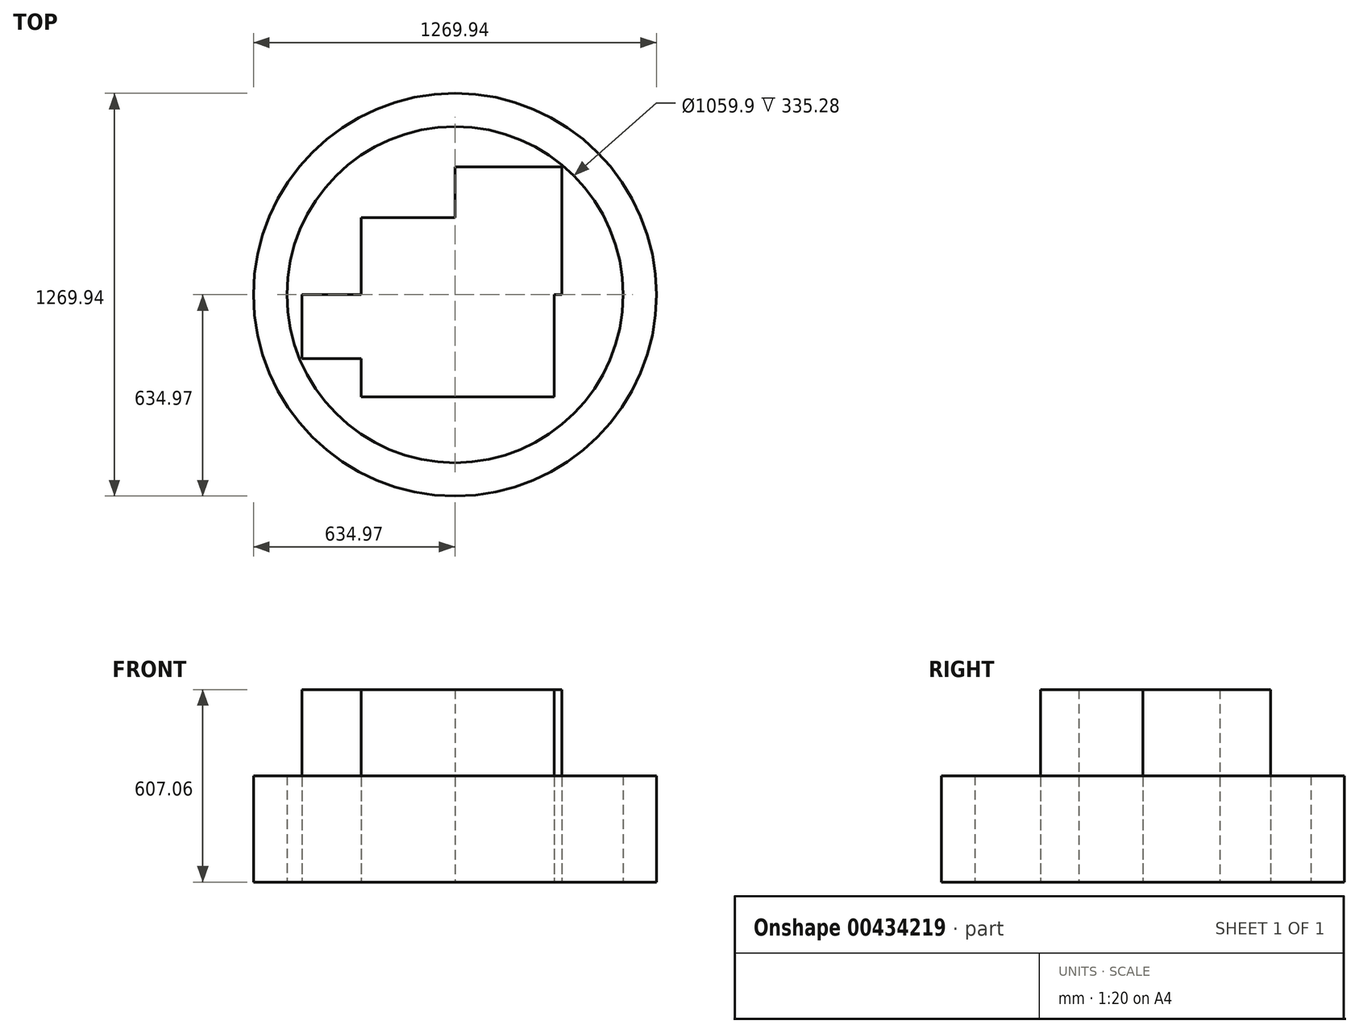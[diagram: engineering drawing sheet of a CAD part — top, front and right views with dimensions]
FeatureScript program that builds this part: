
annotation { "Feature Type Name" : "Feature", "Feature Type Description" : "" }
export const myFeature = defineFeature(function(context is Context, id is Id, definition is map)
    precondition{}
    {
        {
            var Q0;
            Q0=qCreatedBy(makeId("Top.planeOp"),FACE);
            var sketch = newSketch(context, id + "F0", { "sketchPlane" : qUnion([Q0])});
            skCircle(sketch, "E0", {"center": v(0, 0) * mm, "radius": 634.97 * mm});
            skSolve(sketch);
        }
        {
            var Q0;
            Q0 = qSketchRegion(id + "F0", true);
            extrude(context, id + "F1", {"entities" : qUnion([Q0]), "depth" : 335.28 * mm});
        }
        {
            var Q0;
            Q0=qCreatedBy(makeId("Top.planeOp"),FACE);
            var sketch = newSketch(context, id + "F2", { "sketchPlane" : qUnion([Q0])});
            skCircle(sketch, "E1", {"center": v(0, 0) * mm, "radius": 529.95 * mm});
            skSolve(sketch);
        }
        {
            var Q0;
            Q0 = qSketchRegion(id + "F2", true);
            extrude(context, id + "F3", {"entities" : qUnion([Q0]), "operationType" : NewBodyOperationType.REMOVE, "depth" : 337.82 * mm});
        }
        {
            var Q0;
            Q0=qCreatedBy(makeId("Top.planeOp"),FACE);
            var sketch = newSketch(context, id + "F4", { "sketchPlane" : qUnion([Q0])});
            skLineSegment(sketch, "E2.bottom", {"start": v(0, 0) * mm, "end": v(-482.44, 0) * mm});
            skLineSegment(sketch, "E2.top", {"start": v(0, -201.68) * mm, "end": v(-482.44, -201.68) * mm});
            skLineSegment(sketch, "E2.left", {"start": v(0, 0) * mm, "end": v(0, -201.68) * mm});
            skLineSegment(sketch, "E2.right", {"start": v(-482.44, 0) * mm, "end": v(-482.44, -201.68) * mm});
            skLineSegment(sketch, "E3.bottom", {"start": v(0, 0) * mm, "end": v(336.92, 0) * mm});
            skLineSegment(sketch, "E3.top", {"start": v(0, 402.56) * mm, "end": v(336.92, 402.56) * mm});
            skLineSegment(sketch, "E3.left", {"start": v(0, 0) * mm, "end": v(0, 402.56) * mm});
            skLineSegment(sketch, "E3.right", {"start": v(336.92, 0) * mm, "end": v(336.92, 402.56) * mm});
            skLineSegment(sketch, "E4.bottom", {"start": v(313.2, -321.9) * mm, "end": v(-295.8, -321.9) * mm});
            skLineSegment(sketch, "E4.top", {"start": v(313.2, 242.8) * mm, "end": v(-295.8, 242.8) * mm});
            skLineSegment(sketch, "E4.left", {"start": v(313.2, -321.9) * mm, "end": v(313.2, 242.8) * mm});
            skLineSegment(sketch, "E4.right", {"start": v(-295.8, -321.9) * mm, "end": v(-295.8, 242.8) * mm});
            skSolve(sketch);
        }
        {
            var Q0;
            Q0 = qSketchRegion(id + "F4", true);
            extrude(context, id + "F5", {"entities" : qUnion([Q0]), "depth" : 607.06 * mm});
        }
    });
